# Revit family: Legrand UPS Keor Mod Ri
name_source: partatom
category: Installations électriques
units: mm (PartAtom-declared; Revit-internal decimal feet)

## family parameters
Basée sur le plan de construction = Non
Conserver l'orientation des annotations = Non
Cote de connecteur circulaire = Utiliser le diamètre
Couper avec des vides une fois chargée = Non
Numéro OmniClass = 23.80.10.24.17
Partagée = Non
Repère de localisation dans la pièce = Non
Titre OmniClass = Uninterrupted Power Supply (UPS) Units
Toujours verticalement = Oui
Type d'élément = Normal

## types (2) — shared parameters
Communication Ports = RS485
Depth = 874 mm  [stored 2.86745 ft]
Fabricant = Legrand
Frequency = 50 Hz
General Conditions of Use = https://assets.legrand.com
Height B = 88 mm  [stored 0.288714 ft]
Height C = 46 mm  [stored 0.150919 ft]
Legrand symbol = Oui
Material = STEEL
Number of Poles = 3
Power factor = 0.99
RAL = 9003
Text "legrand" = 40 mm  [stored 0.131234 ft]
URL = https://www.legrand.fr
Voltage Input = 400 V
Voltage Output = 400 V
Width = 447 mm
zero-valued in all types: Elévation par défaut

## per-type parameters (varying)
| type | Active Power | Apparent Power | Current | Height | Height A | Height R | Height T | Modèle | Reference | Weight |
| LEGRAND UPS KEOR MOD RI 25 | 25000 W | 25000 VA | 63 A | 663 mm  [stored 2.1752 ft] | 176 mm  [stored 0.577428 ft] | 220 mm  [stored 0.721785 ft] | 221 mm  [stored 0.725066 ft] | UPS 25 H663 P874 L447 | 311134 | 67.00 kg |
| LEGRAND UPS KEOR MOD RI 50 | 50000 W | 50000 VA | 126 A | 930 mm  [stored 3.05118 ft] | 264 mm | 178 mm | 442 mm | UPS 50 H930 P874 L447 | 311135 | 72.00 kg |

note: column(s) folded — value = type name in every type: Product name

note: [stored X ft] marks values corroborated as IEEE doubles in the binary element streams (Revit-internal decimal feet)
